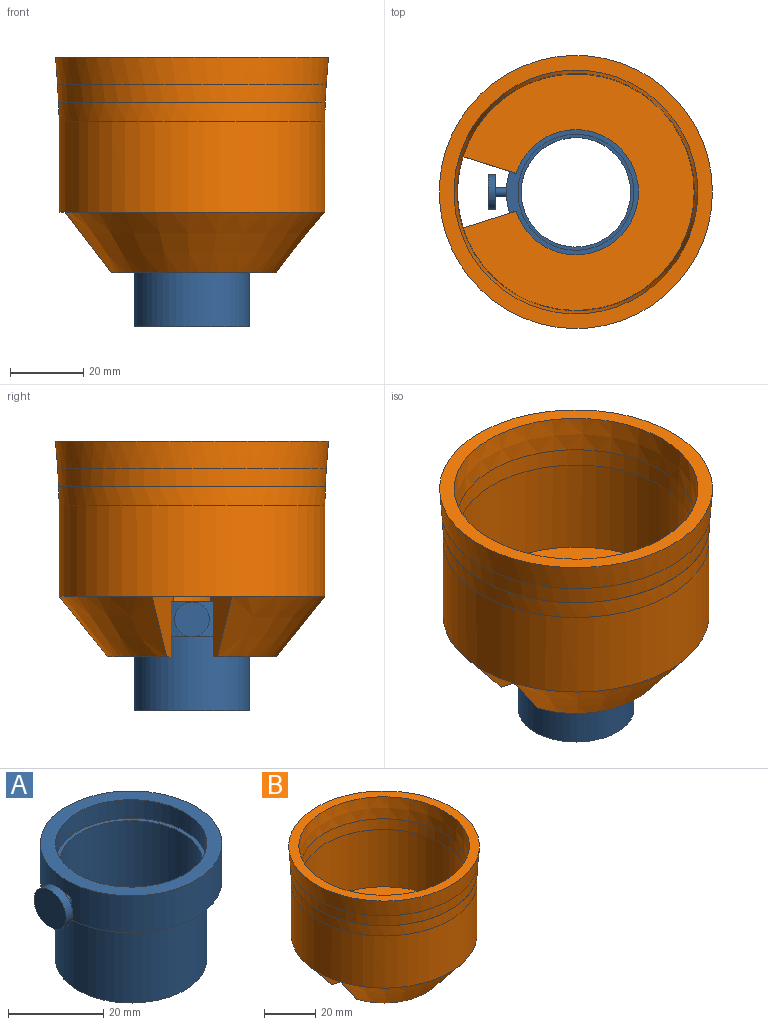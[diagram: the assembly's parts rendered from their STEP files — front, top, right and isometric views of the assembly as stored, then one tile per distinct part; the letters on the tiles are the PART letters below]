
ASSEMBLY  parts=2 mates=1
PART A: 12 faces, bbox 43.1x38.1x29.8 mm
  f0: cylinder r=15.88mm len=31.75mm, axis (0,0,-1), area 475mm2, adj f2,f11
  f1: cylinder r=19.05mm len=38.1mm, axis (0,0,-1), area 1135.2mm2, adj f2,f3,f4
  f2: plane 38.1x38.1mm, normal (0,0,1), area 348.4mm2, adj f0,f1
  f3: plane 38.1x38.1mm, normal (0,0,-1), area 348.4mm2, adj f1,f8
  f4: cylinder r=1.24mm len=3.04mm, axis (-1,0,0), area 23.6mm2, adj f1,f6
  f5: plane 9.51x9.51mm, normal (-1,0,0), area 71.1mm2, adj f7
  f6: plane 9.51x9.51mm, normal (1,0,0), area 66.2mm2, adj f4,f7
  f7: cylinder r=4.76mm len=9.51mm, axis (-1,0,0), area 59.8mm2, adj f5,f6
  f8: cylinder r=15.88mm len=31.75mm, axis (0,0,1), area 2018.6mm2, adj f3,f10
  f9: cylinder r=15mm len=30mm, axis (0,0,1), area 2356.2mm2, adj f10,f11
  f10: plane 31.75x31.75mm, normal (0,0,-1), area 84.9mm2, adj f8,f9
  f11: plane 31.75x31.75mm, normal (0,0,1), area 84.9mm2, adj f0,f9
PART B: 18 faces, bbox 74.8x74.8x59 mm
  f0: plane 64.8x63.3mm, normal (0,0,1), area 2143.1mm2, adj f1,f3,f6,f9
  f1: plane 18.36x16.5mm, normal (-0.3,-0.95,0), area 178.3mm2, adj f0,f2,f4,f5,f6,f7,f10
  f2: cylinder r=19.15mm len=38.3mm, axis (0,0,1), area 1629.4mm2, adj f1,f3,f4,f5
  f3: plane 18.36x16.5mm, normal (-0.3,0.95,0), area 178.3mm2, adj f0,f2,f4,f5,f6,f7,f10
  f4: plane 46.3x45.23mm, normal (0,0,-1), area 479.9mm2, adj f1,f2,f3,f7
  f5: plane 38.3x37.41mm, normal (0,0,-1), area 205.9mm2, adj f1,f2,f3,f6
  f6: cylinder r=17.15mm len=34.3mm, axis (0,0,-1), area 145.9mm2, adj f0,f1,f3,f5
  f7: cone r=36.4mm half-angle=38.8deg, axis (0,0,1), area 3574mm2, adj f1,f3,f4,f11
  f8: cone r=32.4mm half-angle=4.6deg, axis (0,0,1), area 2073.5mm2, adj f13,f14
  f9: cylinder r=32.4mm len=64.8mm, axis (0,0,1), area 5598.3mm2, adj f0,f10,f14
  f10: plane 21.89x5.5mm, normal (0,0,-1), area 84.1mm2, adj f1,f3,f9,f11
  f11: cylinder r=36.4mm len=72.8mm, axis (0,0,1), area 5720mm2, adj f7,f10,f16
  f12: cone r=37.4mm half-angle=4.6deg, axis (0,0,1), area 1750.6mm2, adj f13,f17
  f13: plane 74.8x74.8mm, normal (0,0,1), area 889.7mm2, adj f8,f12
  f14: cone r=32.4mm half-angle=2.3deg, axis (0,0,1), area 1020.2mm2, adj f8,f9
  f15: cone r=36.6mm half-angle=2.3deg, axis (0,0,1), area 3.7mm2, adj f16,f17
  f16: cone r=36.4mm half-angle=1.1deg, axis (0,0,1), area 1140.3mm2, adj f11,f15
  f17: cone r=36.8mm half-angle=3.4deg, axis (0,0,1), area 1146.6mm2, adj f12,f15
PLACE A t=(0,0,9)mm fixed
PLACE B t=(0,0,9)mm
MATE slider B.f2 <-> A.f0  axis (0,0,-1) through (0,0,13.76)mm
